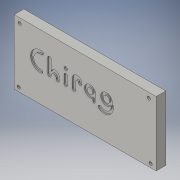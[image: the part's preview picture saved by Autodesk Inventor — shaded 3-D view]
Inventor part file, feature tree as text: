
AUTODESK INVENTOR PART (.ipt)
format: ipt  version: 2016 (Build 200138000, 138)  size: 173,056 bytes
history: native  units: in
note: dims shown in document units (in); Inventor stores cm internally (conversion verified against a paired STEP export)
features: hole x4, sketch x2, extrude x1, emboss x1
ambient origin geometry x8: Origin, YZ Plane, XZ Plane, XY Plane, X Axis, Y Axis, Z Axis, Center Point
bodies: Solid1 (feature_tree)
feature tree (8):
  extrude  "Extrusion1"  Depth=11.0in
  emboss  "Emboss1"
  hole  "Hole1"  [1 undecoded]
  hole  "Hole2"  [1 undecoded]
  hole  "Hole3"  [1 undecoded]
  hole  "Hole4"  [1 undecoded]
  sketch  "Sketch1"  dims[d0=5.0in d1=11.0in]
  sketch  "Sketch2"  dims[d2=0.75in d3=0.0in d4=0.1in d5=0.0in d6=1.0in d7=1.0in d8=0.25in d9=0.75in d10=0.375in d11=0.25in d12=0.5635in d13=1.0in d14=0.8108in d15=1.0in d16=1.0in d17=0.25in d18=0.75in d19=0.375in d20=0.25in d21=0.5635in d22=1.0in d23=0.8108in d24=1.0in d25=1.0in d26=0.25in d27=0.75in d28=0.375in d29=0.25in d30=0.5635in d31=1.0in d32=0.8108in d33=1.0in d34=1.0in d35=0.25in d36=0.75in d37=0.375in d38=0.25in d39=0.5635in d40=1.0in d41=0.8108in]
note: 4 required parameter values undecoded (feature->parameter linkage not recoverable at this tier; creation-order binding heuristic only, values carry confidence <= 0.55)
